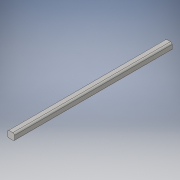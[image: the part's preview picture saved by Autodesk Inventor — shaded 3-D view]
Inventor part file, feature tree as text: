
AUTODESK INVENTOR PART (.ipt)
format: ipt  version: 2016 (Build 200138000, 138)  size: 99,328 bytes
history: native  units: in
note: dims shown in document units (in); Inventor stores cm internally (conversion verified against a paired STEP export)
features: fillet x2, extrude x1, sketch x1
ambient origin geometry x8: Origin, YZ Plane, XZ Plane, XY Plane, X Axis, Y Axis, Z Axis, Center Point
bodies: Solid1 (feature_tree)
feature tree (4):
  extrude  "Extrusion1"  Depth=1.0in
  fillet  "Fillet1"  Radius=24.0in
  fillet  "Fillet2"  Radius=0.125in
  sketch  "Sketch1"  dims[d0=1.0in d1=1.0in d2=24.0in d3=0.0in d4=0.125in d5=0.25in]
